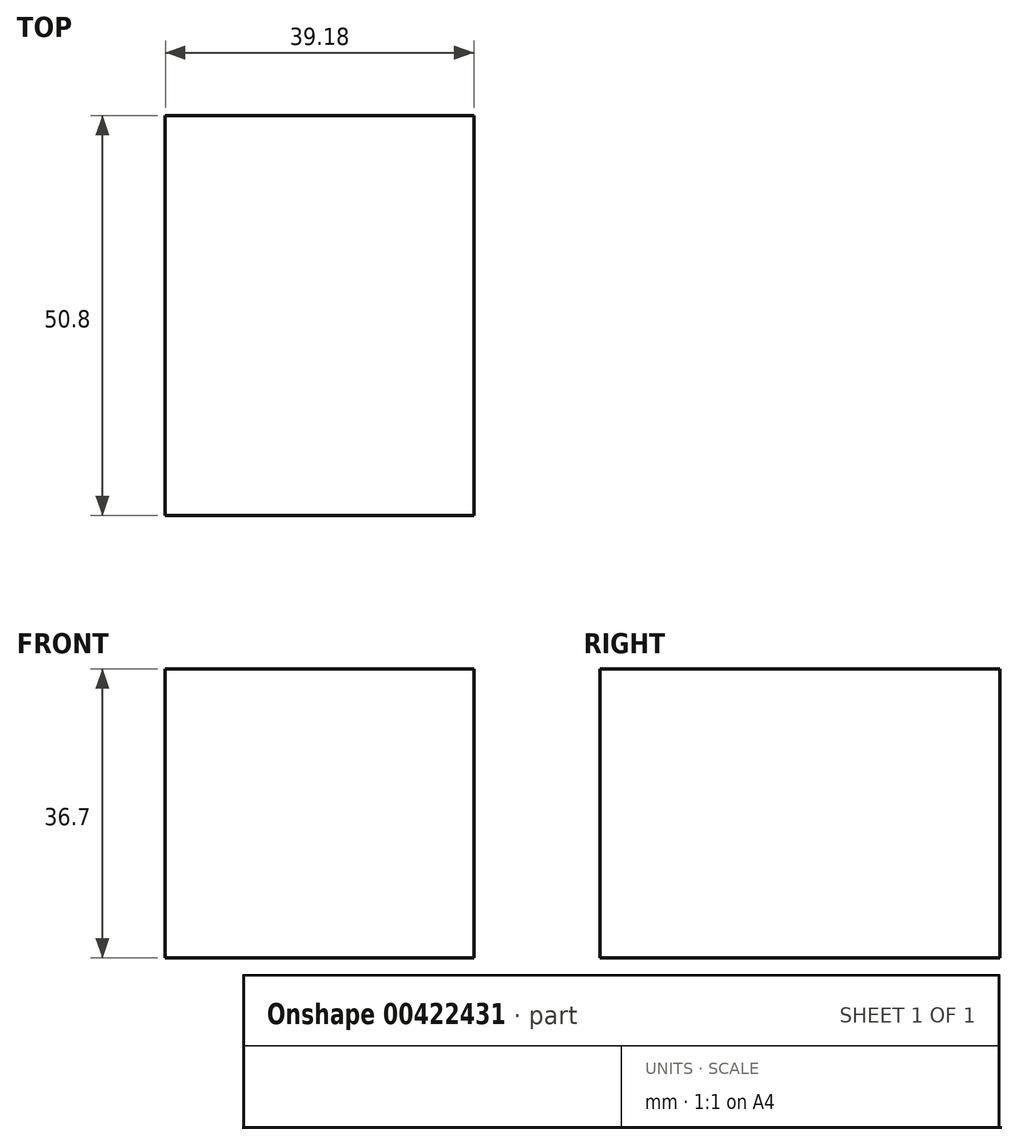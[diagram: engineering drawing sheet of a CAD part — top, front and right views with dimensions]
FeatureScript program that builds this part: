
annotation { "Feature Type Name" : "Feature", "Feature Type Description" : "" }
export const myFeature = defineFeature(function(context is Context, id is Id, definition is map)
    precondition{}
    {
        {
            var Q0;
            Q0=qCreatedBy(makeId("Front.planeOp"),FACE);
            var sketch = newSketch(context, id + "F0", { "sketchPlane" : qUnion([Q0])});
            skLineSegment(sketch, "E0.bottom", {"start": v(19.6, 18.35) * mm, "end": v(-19.6, 18.35) * mm});
            skLineSegment(sketch, "E0.top", {"start": v(19.6, -18.35) * mm, "end": v(-19.6, -18.35) * mm});
            skLineSegment(sketch, "E0.left", {"start": v(19.6, 18.35) * mm, "end": v(19.6, -18.35) * mm});
            skLineSegment(sketch, "E0.right", {"start": v(-19.6, 18.35) * mm, "end": v(-19.6, -18.35) * mm});
            skPoint(sketch, "E0.middle", {"position": v(0, 0) * mm});
            skSolve(sketch);
        }
        {
            var Q0;
            Q0=makeQuery(id+"F0.imprint","IMPRINT",FACE,{"disambiguationData":[TD([[makeQuery(id+"F0.imprint","IMPRINT",EDGE,{"derivedFrom":sQuery(id+"F0.wireOp",EDGE,"AwQYNien-Lfxa-TUjk-9nA6-8B1jxbdK9lur")}),1.0]])]});
            var Q1;
            Q1=makeQuery(id+"F0.imprint","IMPRINT",FACE,{"disambiguationData":[TD([[makeQuery(id+"F0.imprint","IMPRINT",EDGE,{"derivedFrom":sQuery(id+"F0.wireOp",EDGE,"E0.bottom")}),1.0]])]});
            extrude(context, id + "F1", {"entities" : qUnion([Q0, Q1]), "depth" : 50.8 * mm});
        }
    });
